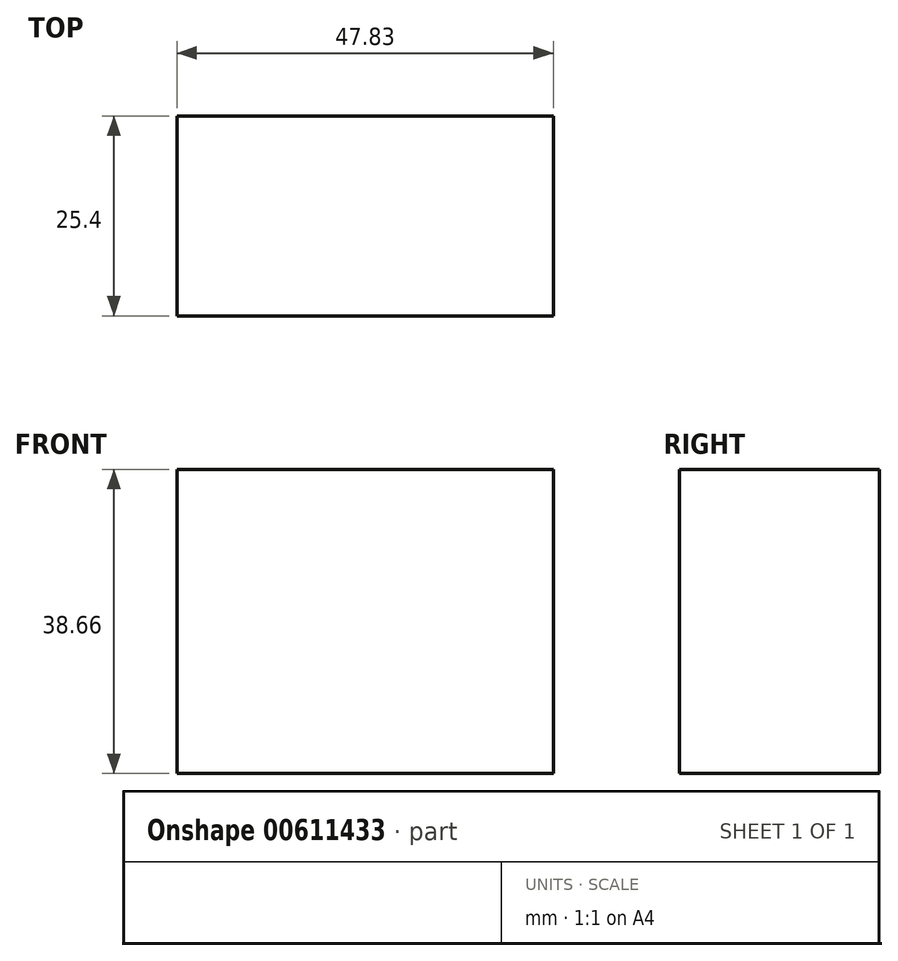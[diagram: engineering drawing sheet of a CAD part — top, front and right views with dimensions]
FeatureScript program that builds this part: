
annotation { "Feature Type Name" : "Feature", "Feature Type Description" : "" }
export const myFeature = defineFeature(function(context is Context, id is Id, definition is map)
    precondition{}
    {
        {
            var Q0;
            Q0=qCreatedBy(makeId("Front.planeOp"),FACE);
            var sketch = newSketch(context, id + "F0", { "sketchPlane" : qUnion([Q0])});
            skLineSegment(sketch, "E0.bottom", {"start": v(0, 0) * mm, "end": v(47.83, 0) * mm});
            skLineSegment(sketch, "E0.top", {"start": v(0, 38.66) * mm, "end": v(47.83, 38.66) * mm});
            skLineSegment(sketch, "E0.left", {"start": v(0, 0) * mm, "end": v(0, 38.66) * mm});
            skLineSegment(sketch, "E0.right", {"start": v(47.83, 0) * mm, "end": v(47.83, 38.66) * mm});
            skSolve(sketch);
        }
        {
            var Q0;
            Q0 = qSketchRegion(id + "F0", true);
            extrude(context, id + "F1", {"entities" : qUnion([Q0]), "depth" : 25.4 * mm, "offsetDistance" : 25.4 * mm});
        }
    });
